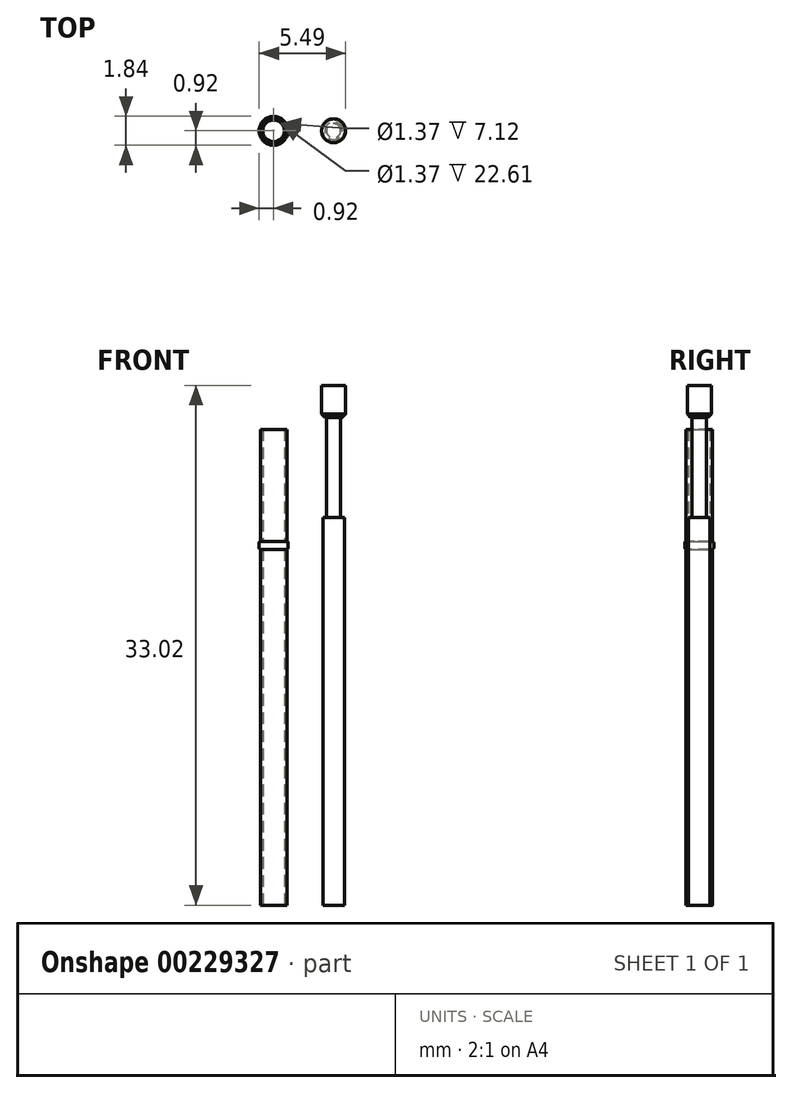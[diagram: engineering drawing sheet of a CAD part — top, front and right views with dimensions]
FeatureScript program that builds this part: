
annotation { "Feature Type Name" : "Feature", "Feature Type Description" : "" }
export const myFeature = defineFeature(function(context is Context, id is Id, definition is map)
    precondition{}
    {
        {
            var Q0;
            Q0=qCreatedBy(makeId("Top.planeOp"),FACE);
            var sketch = newSketch(context, id + "F0", { "sketchPlane" : qUnion([Q0])});
            skCircle(sketch, "E0", {"center": v(0, 0) * mm, "radius": 0.84 * mm});
            skCircle(sketch, "E1", {"center": v(0, 0) * mm, "radius": 0.69 * mm});
            skSolve(sketch);
        }
        {
            var Q0;
            Q0 = qSketchRegion(id + "F0", true);
            extrude(context, id + "F1", {"entities" : qUnion([Q0]), "depth" : 30.23 * mm});
        }
        {
            var Q0;
            Q0=qCreatedBy(makeId("Top.planeOp"),FACE);
            var sketch = newSketch(context, id + "F2", { "sketchPlane" : qUnion([Q0])});
            skCircle(sketch, "E2", {"center": v(3.81, 0) * mm, "radius": 0.69 * mm});
            skSolve(sketch);
        }
        {
            var Q0;
            Q0 = qSketchRegion(id + "F2", true);
            extrude(context, id + "F3", {"entities" : qUnion([Q0]), "depth" : 24.64 * mm});
        }
        {
            var Q0;
            Q0=makeQuery(id+"F3.opExtrude","CAP_FACE",FACE,{"disambiguationData":[OSD([sQuery(id+"F2.wireOp",EDGE,"E2")])],"isStart":false});
            var sketch = newSketch(context, id + "F4", { "sketchPlane" : qUnion([Q0])});
            skCircle(sketch, "E3", {"center": v(3.81, 0) * mm, "radius": 0.46 * mm});
            skSolve(sketch);
        }
        {
            var Q0;
            Q0 = qSketchRegion(id + "F4", true);
            extrude(context, id + "F5", {"entities" : qUnion([Q0]), "operationType" : NewBodyOperationType.ADD, "depth" : 6.35 * mm});
        }
        {
            var Q0;
            Q0=makeQuery(id+"F5.opExtrude","CAP_FACE",FACE,{"disambiguationData":[OSD([sQuery(id+"F4.wireOp",EDGE,"E3")])],"isStart":false});
            var sketch = newSketch(context, id + "F6", { "sketchPlane" : qUnion([Q0])});
            skCircle(sketch, "E4", {"center": v(3.81, 0) * mm, "radius": 0.76 * mm});
            skSolve(sketch);
        }
        {
            var Q0;
            Q0 = qSketchRegion(id + "F6", true);
            extrude(context, id + "F7", {"entities" : qUnion([Q0]), "operationType" : NewBodyOperationType.ADD, "depth" : 2.03 * mm});
        }
        {
            var Q0;
            Q0=makeQuery(id+"F7.opExtrude","CAP_EDGE",EDGE,{"disambiguationData":[OSD([sQuery(id+"F6.wireOp",EDGE,"E4")])],"isStart":true});
            chamfer(context, id + "F8", {"entities" : qUnion([Q0]), "width" : .2 * mm, "tangentPropagation" : true});
        }
        {
            var Q0;
            Q0=qCreatedBy(makeId("Front.planeOp"),FACE);
            var sketch = newSketch(context, id + "F9", { "sketchPlane" : qUnion([Q0])});
            skLineSegment(sketch, "E5", {"start": v(0, 23.1) * mm, "end": v(-0.92, 23.1) * mm});
            skLineSegment(sketch, "E6", {"start": v(-0.92, 23.1) * mm, "end": v(-0.92, 22.6) * mm});
            skLineSegment(sketch, "E7", {"start": v(-0.92, 22.6) * mm, "end": v(0, 22.6) * mm});
            skLineSegment(sketch, "E8", {"start": v(0, 23.1) * mm, "end": v(0, 22.6) * mm});
            skSolve(sketch);
        }
        {
            var Q0;
            Q0 = qSketchRegion(id + "F9", true);
            var Q1;
            Q1=sQuery(id+"F9.wireOp",EDGE,"E8");
            revolve(context, id + "F10", {"operationType" : NewBodyOperationType.ADD, "entities" : qUnion([Q0]), "axis" : qUnion([Q1]), "revolveType" : RevolveType.FULL});
        }
        {
            var Q0;
            Q0=makeQuery(id+"F10.opRevolve","SWEPT_EDGE",EDGE,{"disambiguationData":[OSD([sQuery(id+"F9.wireOp",EDGE,"E5"),sQuery(id+"F9.wireOp",EDGE,"E6")])]});
            var Q1;
            Q1=makeQuery(id+"F10.opRevolve","SWEPT_EDGE",EDGE,{"disambiguationData":[OSD([sQuery(id+"F9.wireOp",EDGE,"E6"),sQuery(id+"F9.wireOp",EDGE,"E7")])]});
            fillet(context, id + "F11", {"entities" : qUnion([Q0, Q1]), "radius" : .1 * mm, "tangentPropagation" : true, "allowEdgeOverflow" : false});
        }
    });
